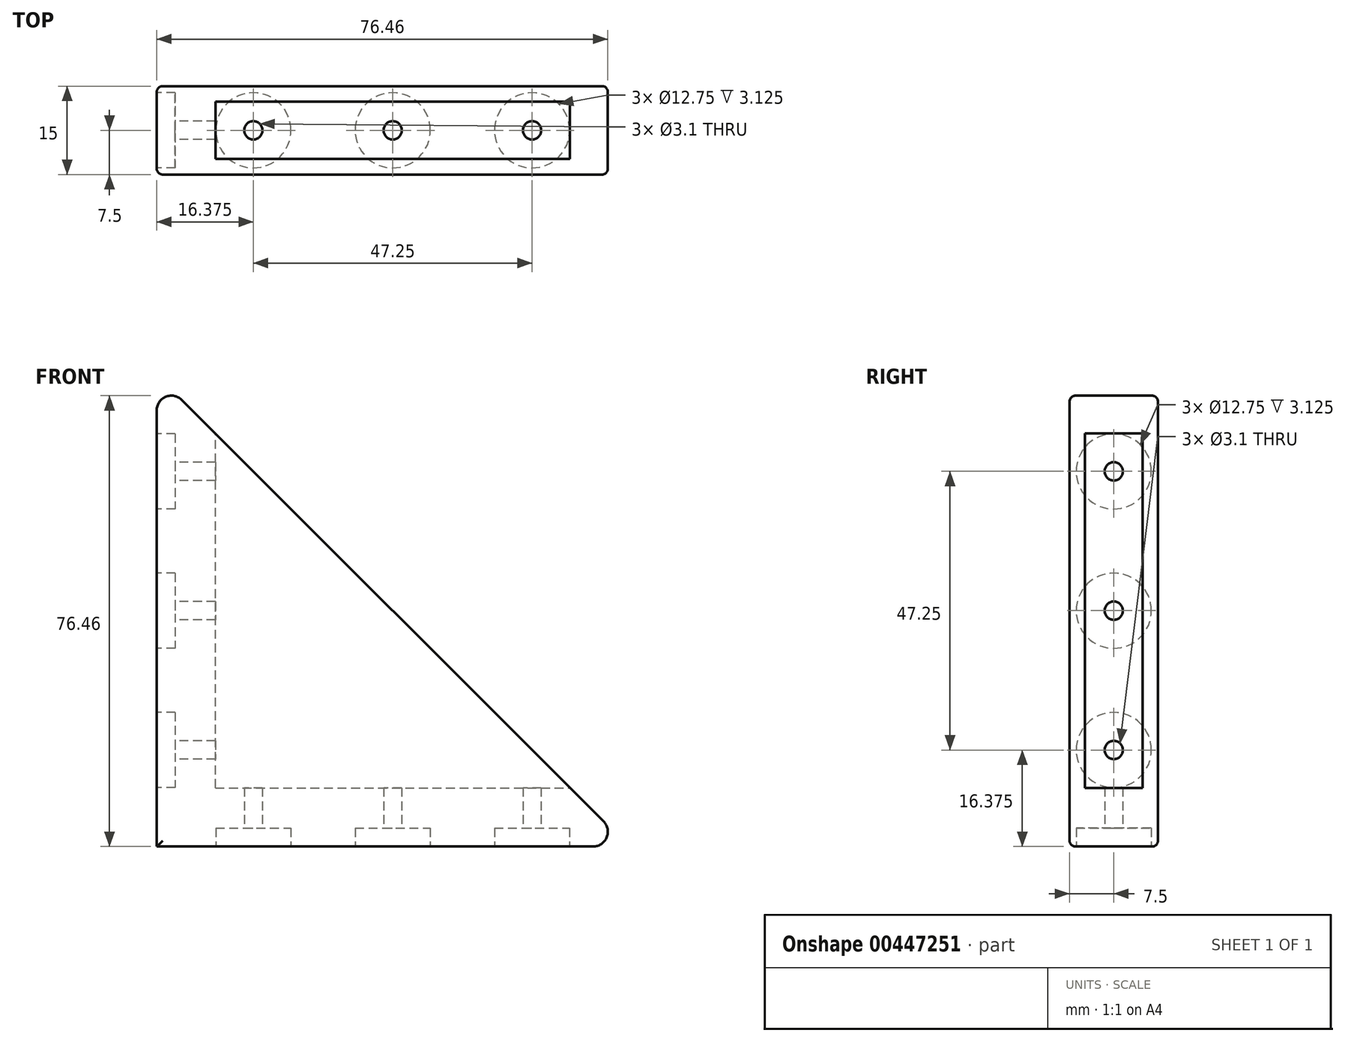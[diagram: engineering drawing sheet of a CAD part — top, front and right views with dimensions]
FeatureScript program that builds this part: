
annotation { "Feature Type Name" : "Feature", "Feature Type Description" : "" }
export const myFeature = defineFeature(function(context is Context, id is Id, definition is map)
    precondition{}
    {
        {
            var Q0;
            Q0=qCreatedBy(makeId("Front.planeOp"),FACE);
            var sketch = newSketch(context, id + "F0", { "sketchPlane" : qUnion([Q0])});
            skLineSegment(sketch, "E0", {"start": v(0, 80) * mm, "end": v(0, 0) * mm});
            skLineSegment(sketch, "E1", {"start": v(0, 0) * mm, "end": v(80, 0) * mm});
            skLineSegment(sketch, "E2", {"start": v(80, 0) * mm, "end": v(0, 80) * mm});
            skSolve(sketch);
        }
        {
            var Q0;
            Q0=makeQuery(id+"F0.imprint","IMPRINT",FACE,{"disambiguationData":[TD([[makeQuery(id+"F0.imprint","IMPRINT",EDGE,{"derivedFrom":sQuery(id+"F0.wireOp",EDGE,"E0")}),1.0]])]});
            extrude(context, id + "F1", {"entities" : qUnion([Q0]), "endBound" : BoundingType.SYMMETRIC, "depth" : 15 * mm});
        }
        {
            var Q0;
            Q0=makeQuery(id+"F1.opExtrude","SWEPT_FACE",FACE,{"disambiguationData":[OSD([sQuery(id+"F0.wireOp",EDGE,"E0")])]});
            var sketch = newSketch(context, id + "F2", { "sketchPlane" : qUnion([Q0])});
            skCircle(sketch, "E3", {"center": v(0, 16.38) * mm, "radius": 6.38 * mm});
            skCircle(sketch, "E4.0.1.0", {"center": v(0, 40) * mm, "radius": 6.38 * mm});
            skCircle(sketch, "E4.0.2.0", {"center": v(0, 63.62) * mm, "radius": 6.38 * mm});
            skLineSegment(sketch, "E4.direction1", {"start": v(0, 16.38) * mm, "end": v(25, 16.38) * mm, "construction": true});
            skLineSegment(sketch, "E4.direction2", {"start": v(0, 16.38) * mm, "end": v(0, 40) * mm, "construction": true});
            skSolve(sketch);
        }
        {
            var Q0;
            Q0=makeQuery(id+"F2.imprint","IMPRINT",FACE,{"disambiguationData":[TD([[makeQuery(id+"F2.imprint","IMPRINT",EDGE,{"derivedFrom":sQuery(id+"F2.wireOp",EDGE,"E4.0.2.0")}),1.0]])]});
            var Q1;
            Q1=makeQuery(id+"F2.imprint","IMPRINT",FACE,{"disambiguationData":[TD([[makeQuery(id+"F2.imprint","IMPRINT",EDGE,{"derivedFrom":sQuery(id+"F2.wireOp",EDGE,"E4.0.1.0")}),1.0]])]});
            var Q2;
            Q2=makeQuery(id+"F2.imprint","IMPRINT",FACE,{"disambiguationData":[TD([[makeQuery(id+"F2.imprint","IMPRINT",EDGE,{"derivedFrom":sQuery(id+"F2.wireOp",EDGE,"E3")}),1.0]])]});
            extrude(context, id + "F3", {"entities" : qUnion([Q0, Q1, Q2]), "operationType" : NewBodyOperationType.REMOVE, "oppositeDirection" : true, "depth" : 3.12 * mm});
        }
        {
            var Q0;
            Q0=makeQuery(id+"F1.opExtrude","SWEPT_FACE",FACE,{"disambiguationData":[OSD([sQuery(id+"F0.wireOp",EDGE,"E1")])]});
            var sketch = newSketch(context, id + "F4", { "sketchPlane" : qUnion([Q0])});
            skCircle(sketch, "E5", {"center": v(16.38, 0) * mm, "radius": 6.38 * mm});
            skCircle(sketch, "E6.1.0.0", {"center": v(40, 0) * mm, "radius": 6.38 * mm});
            skCircle(sketch, "E6.2.0.0", {"center": v(63.62, 0) * mm, "radius": 6.38 * mm});
            skLineSegment(sketch, "E6.direction1", {"start": v(16.38, 0) * mm, "end": v(40, 0) * mm, "construction": true});
            skSolve(sketch);
        }
        {
            var Q0;
            Q0=makeQuery(id+"F4.imprint","IMPRINT",FACE,{"disambiguationData":[TD([[makeQuery(id+"F4.imprint","IMPRINT",EDGE,{"derivedFrom":sQuery(id+"F4.wireOp",EDGE,"E5")}),1.0]])]});
            var Q1;
            Q1=makeQuery(id+"F4.imprint","IMPRINT",FACE,{"disambiguationData":[TD([[makeQuery(id+"F4.imprint","IMPRINT",EDGE,{"derivedFrom":sQuery(id+"F4.wireOp",EDGE,"E6.1.0.0")}),1.0]])]});
            var Q2;
            Q2=makeQuery(id+"F4.imprint","IMPRINT",FACE,{"disambiguationData":[TD([[makeQuery(id+"F4.imprint","IMPRINT",EDGE,{"derivedFrom":sQuery(id+"F4.wireOp",EDGE,"E6.2.0.0")}),1.0]])]});
            extrude(context, id + "F5", {"entities" : qUnion([Q0, Q1, Q2]), "operationType" : NewBodyOperationType.REMOVE, "oppositeDirection" : true, "depth" : 3.12 * mm});
        }
        {
            var Q0;
            Q0=qCreatedBy(makeId("Front.planeOp"),FACE);
            var sketch = newSketch(context, id + "F6", { "sketchPlane" : qUnion([Q0])});
            skLineSegment(sketch, "E7.bottom", {"start": v(9.95, 9.95) * mm, "end": v(70.05, 9.95) * mm});
            skLineSegment(sketch, "E7.top", {"start": v(9.95, 70.05) * mm, "end": v(70.05, 70.05) * mm});
            skLineSegment(sketch, "E7.left", {"start": v(9.95, 9.95) * mm, "end": v(9.95, 70.05) * mm});
            skLineSegment(sketch, "E7.right", {"start": v(70.05, 9.95) * mm, "end": v(70.05, 70.05) * mm});
            skLineSegment(sketch, "E8.0", {"start": v(80, 0) * mm, "end": v(0, 80) * mm, "construction": true});
            skLineSegment(sketch, "E9", {"start": v(0, 0) * mm, "end": v(40, 40) * mm, "construction": true});
            skSolve(sketch);
        }
        {
            var Q0;
            Q0=makeQuery(id+"F6.imprint","IMPRINT",FACE,{"disambiguationData":[TD([[makeQuery(id+"F6.imprint","IMPRINT",EDGE,{"derivedFrom":sQuery(id+"F6.wireOp",EDGE,"E7.bottom")}),1.0]])]});
            extrude(context, id + "F7", {"entities" : qUnion([Q0]), "operationType" : NewBodyOperationType.REMOVE, "endBound" : BoundingType.SYMMETRIC, "depth" : 9.75 * mm});
        }
        {
            var Q0;
            Q0=makeQuery(id+"F3.boolean.opBoolean","COPY",FACE,{"derivedFrom":makeQuery(id+"F3.opExtrude","CAP_FACE",FACE,{"disambiguationData":[OSD([sQuery(id+"F2.wireOp",EDGE,"E4.0.2.0")])],"isStart":false})});
            var sketch = newSketch(context, id + "F8", { "sketchPlane" : qUnion([Q0])});
            skCircle(sketch, "E10.0", {"center": v(0, 63.62) * mm, "radius": 6.38 * mm});
            skCircle(sketch, "E11.0", {"center": v(0, 40) * mm, "radius": 6.38 * mm});
            skCircle(sketch, "E12.0", {"center": v(0, 16.38) * mm, "radius": 6.38 * mm});
            skCircle(sketch, "E13", {"center": v(0, 63.62) * mm, "radius": 1.55 * mm});
            skCircle(sketch, "E14", {"center": v(0, 40) * mm, "radius": 1.55 * mm});
            skCircle(sketch, "E15", {"center": v(0, 16.38) * mm, "radius": 1.55 * mm});
            skSolve(sketch);
        }
        {
            var Q0;
            Q0=makeQuery(id+"F8.imprint","IMPRINT",FACE,{"disambiguationData":[TD([[makeQuery(id+"F8.imprint","IMPRINT",EDGE,{"derivedFrom":sQuery(id+"F8.wireOp",EDGE,"E13")}),1.0]])]});
            var Q1;
            Q1=makeQuery(id+"F8.imprint","IMPRINT",FACE,{"disambiguationData":[TD([[makeQuery(id+"F8.imprint","IMPRINT",EDGE,{"derivedFrom":sQuery(id+"F8.wireOp",EDGE,"E14")}),1.0]])]});
            var Q2;
            Q2=makeQuery(id+"F8.imprint","IMPRINT",FACE,{"disambiguationData":[TD([[makeQuery(id+"F8.imprint","IMPRINT",EDGE,{"derivedFrom":sQuery(id+"F8.wireOp",EDGE,"E15")}),1.0]])]});
            extrude(context, id + "F9", {"entities" : qUnion([Q0, Q1, Q2]), "operationType" : NewBodyOperationType.REMOVE, "endBound" : BoundingType.THROUGH_ALL, "oppositeDirection" : true, "depth" : 25 * mm});
        }
        {
            var Q0;
            Q0=makeQuery(id+"F5.boolean.opBoolean","COPY",FACE,{"derivedFrom":makeQuery(id+"F5.opExtrude","CAP_FACE",FACE,{"disambiguationData":[OSD([sQuery(id+"F4.wireOp",EDGE,"E5")])],"isStart":false})});
            var sketch = newSketch(context, id + "F10", { "sketchPlane" : qUnion([Q0])});
            skCircle(sketch, "E16.0", {"center": v(16.38, 0) * mm, "radius": 6.38 * mm});
            skCircle(sketch, "E17.0", {"center": v(40, 0) * mm, "radius": 6.38 * mm});
            skCircle(sketch, "E18.0", {"center": v(63.62, 0) * mm, "radius": 6.38 * mm});
            skCircle(sketch, "E19", {"center": v(16.38, 0) * mm, "radius": 1.55 * mm});
            skCircle(sketch, "E20", {"center": v(40, 0) * mm, "radius": 1.55 * mm});
            skCircle(sketch, "E21", {"center": v(63.62, 0) * mm, "radius": 1.55 * mm});
            skSolve(sketch);
        }
        {
            var Q0;
            Q0=makeQuery(id+"F10.imprint","IMPRINT",FACE,{"disambiguationData":[TD([[makeQuery(id+"F10.imprint","IMPRINT",EDGE,{"derivedFrom":sQuery(id+"F10.wireOp",EDGE,"E19")}),1.0]])]});
            var Q1;
            Q1=makeQuery(id+"F10.imprint","IMPRINT",FACE,{"disambiguationData":[TD([[makeQuery(id+"F10.imprint","IMPRINT",EDGE,{"derivedFrom":sQuery(id+"F10.wireOp",EDGE,"E20")}),1.0]])]});
            var Q2;
            Q2=makeQuery(id+"F10.imprint","IMPRINT",FACE,{"disambiguationData":[TD([[makeQuery(id+"F10.imprint","IMPRINT",EDGE,{"derivedFrom":sQuery(id+"F10.wireOp",EDGE,"E21")}),1.0]])]});
            extrude(context, id + "F11", {"entities" : qUnion([Q0, Q1, Q2]), "operationType" : NewBodyOperationType.REMOVE, "endBound" : BoundingType.THROUGH_ALL, "oppositeDirection" : true, "depth" : 25 * mm});
        }
        {
            var Q0;
            Q0=makeQuery(id+"F1.opExtrude","SWEPT_EDGE",EDGE,{"disambiguationData":[OSD([sQuery(id+"F0.wireOp",EDGE,"E0"),sQuery(id+"F0.wireOp",EDGE,"E2")])]});
            var Q1;
            Q1=makeQuery(id+"F1.opExtrude","SWEPT_EDGE",EDGE,{"disambiguationData":[OSD([sQuery(id+"F0.wireOp",EDGE,"E1"),sQuery(id+"F0.wireOp",EDGE,"E2")])]});
            fillet(context, id + "F12", {"entities" : qUnion([Q0, Q1]), "radius" : 2.5 * mm, "tangentPropagation" : true, "allowEdgeOverflow" : false});
        }
        {
            var Q0;
            Q0=makeQuery(id+"F1.opExtrude","CAP_EDGE",EDGE,{"disambiguationData":[OSD([sQuery(id+"F0.wireOp",EDGE,"E2")])],"isStart":false});
            var Q1;
            Q1=makeQuery(id+"F1.opExtrude","CAP_EDGE",EDGE,{"disambiguationData":[OSD([sQuery(id+"F0.wireOp",EDGE,"E2")])],"isStart":true});
            fillet(context, id + "F13", {"entities" : qUnion([Q0, Q1]), "radius" : 1 * mm, "tangentPropagation" : true, "allowEdgeOverflow" : false});
        }
    });
